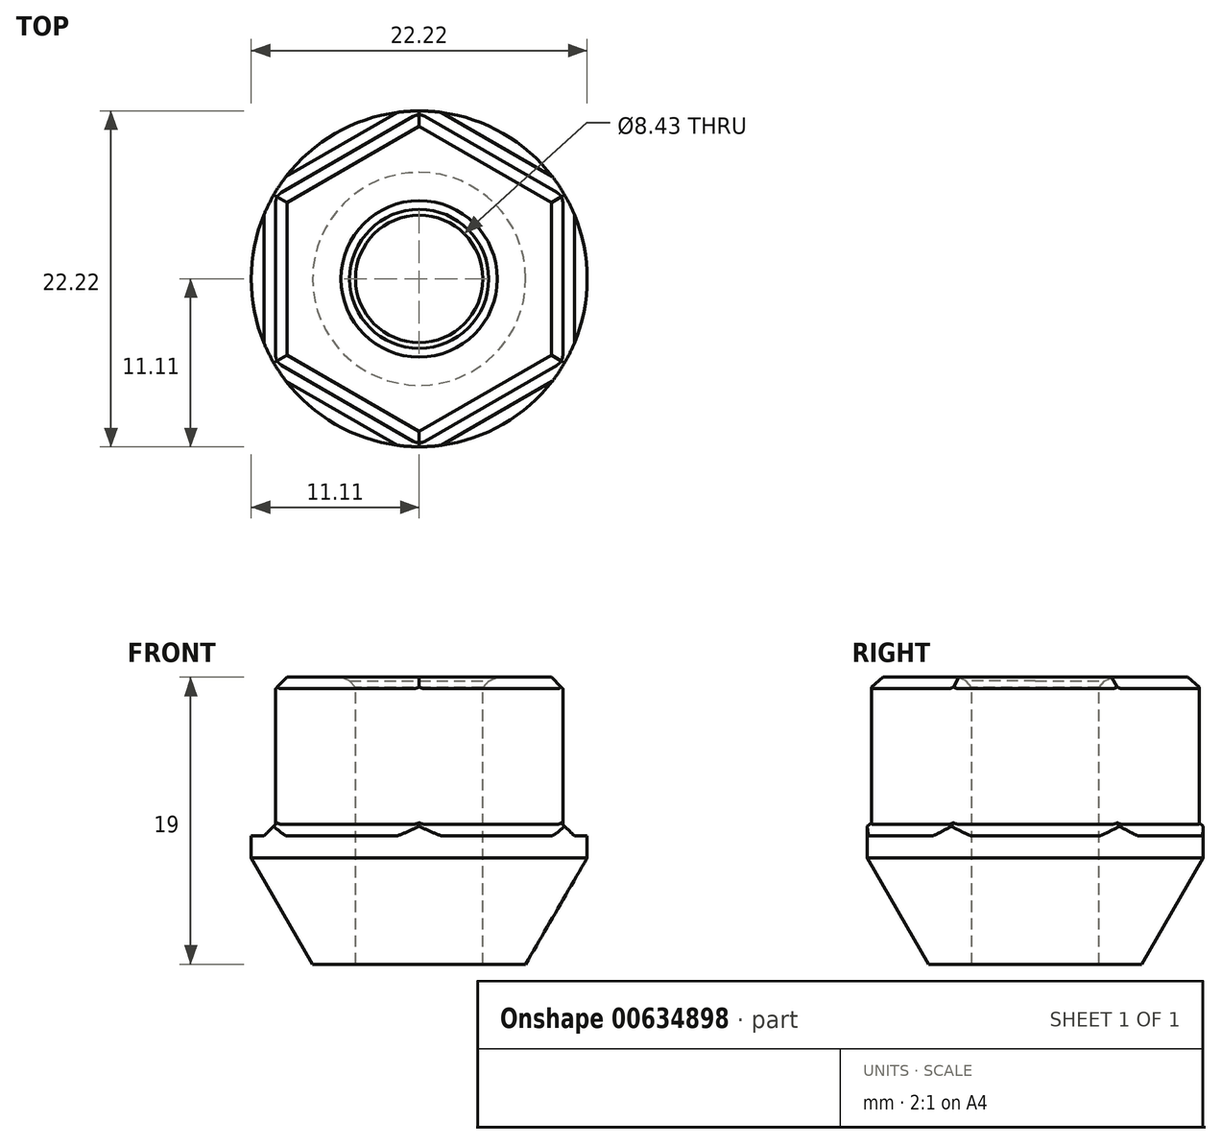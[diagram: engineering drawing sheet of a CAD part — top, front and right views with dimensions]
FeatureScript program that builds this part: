
annotation { "Feature Type Name" : "Feature", "Feature Type Description" : "" }
export const myFeature = defineFeature(function(context is Context, id is Id, definition is map)
    precondition{}
    {
        {
            var Q0;
            Q0=qCreatedBy(makeId("Top.planeOp"),FACE);
            var sketch = newSketch(context, id + "F0", { "sketchPlane" : qUnion([Q0])});
            skCircle(sketch, "E0.cCircle", {"center": v(0, 0) * mm, "radius": 9.5 * mm, "construction": true});
            skLineSegment(sketch, "E0.0", {"start": v(9.5, 5.48) * mm, "end": v(9.5, -5.48) * mm});
            skLineSegment(sketch, "E0.1", {"start": v(9.5, -5.48) * mm, "end": v(0, -10.97) * mm});
            skLineSegment(sketch, "E0.2", {"start": v(0, -10.97) * mm, "end": v(-9.5, -5.48) * mm});
            skLineSegment(sketch, "E0.3", {"start": v(-9.5, -5.48) * mm, "end": v(-9.5, 5.48) * mm});
            skLineSegment(sketch, "E0.4", {"start": v(-9.5, 5.48) * mm, "end": v(0, 10.97) * mm});
            skLineSegment(sketch, "E0.5", {"start": v(0, 10.97) * mm, "end": v(9.5, 5.48) * mm});
            skPoint(sketch, "E0.0.midPoint", {"position": v(9.5, 0) * mm});
            skSolve(sketch);
        }
        {
            var Q0;
            Q0 = qSketchRegion(id + "F0", true);
            extrude(context, id + "F1", {"entities" : qUnion([Q0]), "oppositeDirection" : true, "depth" : 19 * mm, "offsetDistance" : 25.4 * mm});
        }
        {
            var Q0;
            Q0=sQuery(id+"F0.wireOp",VERTEX,"E0.cCircle.center");
            var Q1;
            Q1=makeQuery(id+"F1.opExtrude","SWEPT_BODY",BODY,{"disambiguationData":[OSD([sQuery(id+"F0.wireOp",EDGE,"E0.0"),sQuery(id+"F0.wireOp",EDGE,"E0.1"),sQuery(id+"F0.wireOp",EDGE,"E0.2"),sQuery(id+"F0.wireOp",EDGE,"E0.3"),sQuery(id+"F0.wireOp",EDGE,"E0.4"),sQuery(id+"F0.wireOp",EDGE,"E0.5")])]});
            hole(context, id + "F2", {"style" : HoleStyle.C_SINK, "endStyle" : HoleEndStyle.THROUGH, "holeDiameter" : 8.43 * mm, "cSinkDiameter" : 9.65 * mm, "cSinkAngle" : 82 * degree, "majorDiameter" : 9.52 * mm, "isTappedThrough" : true, "tappedDepth" : 3.56 * mm, "tapClearance" : 3, "startFromSketch" : true, "locations" : qUnion([Q0]), "scope" : qUnion([Q1])});
        }
        {
            var Q0;
            Q0=makeQuery(id+"F1.opExtrude","CAP_FACE",FACE,{"disambiguationData":[OSD([sQuery(id+"F0.wireOp",EDGE,"E0.0"),sQuery(id+"F0.wireOp",EDGE,"E0.1"),sQuery(id+"F0.wireOp",EDGE,"E0.2"),sQuery(id+"F0.wireOp",EDGE,"E0.3"),sQuery(id+"F0.wireOp",EDGE,"E0.4"),sQuery(id+"F0.wireOp",EDGE,"E0.5")])],"isStart":false});
            var sketch = newSketch(context, id + "F3", { "sketchPlane" : qUnion([Q0])});
            skCircle(sketch, "E1", {"center": v(0, 0) * mm, "radius": 11.11 * mm});
            skCircle(sketch, "E2.0", {"center": v(0, 0) * mm, "radius": 4.22 * mm});
            skSolve(sketch);
        }
        {
            var Q0;
            Q0 = qSketchRegion(id + "F3", true);
            extrude(context, id + "F4", {"entities" : qUnion([Q0]), "operationType" : NewBodyOperationType.ADD, "oppositeDirection" : true, "depth" : 8.5 * mm, "offsetDistance" : 25.4 * mm});
        }
        {
            var Q0;
            Q0=makeQuery(id+"F4.opExtrude","CAP_EDGE",EDGE,{"disambiguationData":[OSD([sQuery(id+"F3.wireOp",EDGE,"E1")])],"isStart":true});
            chamfer(context, id + "F5", {"entities" : qUnion([Q0]), "chamferType" : ChamferType.OFFSET_ANGLE, "width" : 4.06 * mm, "oppositeDirection" : false, "angle" : 60 * degree, "tangentPropagation" : true});
        }
        {
            var Q0;
            Q0=makeQuery(id+"F1.opExtrude","CAP_FACE",FACE,{"disambiguationData":[OSD([sQuery(id+"F0.wireOp",EDGE,"E0.0"),sQuery(id+"F0.wireOp",EDGE,"E0.1"),sQuery(id+"F0.wireOp",EDGE,"E0.2"),sQuery(id+"F0.wireOp",EDGE,"E0.3"),sQuery(id+"F0.wireOp",EDGE,"E0.4"),sQuery(id+"F0.wireOp",EDGE,"E0.5")])],"isStart":true});
            chamfer(context, id + "F6", {"entities" : qUnion([Q0]), "width" : 0.76 * mm, "tangentPropagation" : true});
        }
        {
            var Q0;
            Q0=makeQuery(id+"F4.boolean.opBoolean","INTERSECT",EDGE,{"derivedFrom":[makeQuery(id+"F1.opExtrude","SWEPT_FACE",FACE,{"disambiguationData":[OSD([sQuery(id+"F0.wireOp",EDGE,"E0.2")])]}),makeQuery(id+"F4.opExtrude","CAP_FACE",FACE,{"disambiguationData":[OSD([sQuery(id+"F3.wireOp",EDGE,"E1"),sQuery(id+"F3.wireOp",EDGE,"E2.0")])],"isStart":false})]});
            var Q1;
            Q1=makeQuery(id+"F4.boolean.opBoolean","INTERSECT",EDGE,{"derivedFrom":[makeQuery(id+"F1.opExtrude","SWEPT_FACE",FACE,{"disambiguationData":[OSD([sQuery(id+"F0.wireOp",EDGE,"E0.1")])]}),makeQuery(id+"F4.opExtrude","CAP_FACE",FACE,{"disambiguationData":[OSD([sQuery(id+"F3.wireOp",EDGE,"E1"),sQuery(id+"F3.wireOp",EDGE,"E2.0")])],"isStart":false})]});
            var Q2;
            Q2=makeQuery(id+"F4.boolean.opBoolean","INTERSECT",EDGE,{"derivedFrom":[makeQuery(id+"F1.opExtrude","SWEPT_FACE",FACE,{"disambiguationData":[OSD([sQuery(id+"F0.wireOp",EDGE,"E0.0")])]}),makeQuery(id+"F4.opExtrude","CAP_FACE",FACE,{"disambiguationData":[OSD([sQuery(id+"F3.wireOp",EDGE,"E1"),sQuery(id+"F3.wireOp",EDGE,"E2.0")])],"isStart":false})]});
            var Q3;
            Q3=makeQuery(id+"F4.boolean.opBoolean","INTERSECT",EDGE,{"derivedFrom":[makeQuery(id+"F1.opExtrude","SWEPT_FACE",FACE,{"disambiguationData":[OSD([sQuery(id+"F0.wireOp",EDGE,"E0.5")])]}),makeQuery(id+"F4.opExtrude","CAP_FACE",FACE,{"disambiguationData":[OSD([sQuery(id+"F3.wireOp",EDGE,"E1"),sQuery(id+"F3.wireOp",EDGE,"E2.0")])],"isStart":false})]});
            var Q4;
            Q4=makeQuery(id+"F4.boolean.opBoolean","INTERSECT",EDGE,{"derivedFrom":[makeQuery(id+"F1.opExtrude","SWEPT_FACE",FACE,{"disambiguationData":[OSD([sQuery(id+"F0.wireOp",EDGE,"E0.4")])]}),makeQuery(id+"F4.opExtrude","CAP_FACE",FACE,{"disambiguationData":[OSD([sQuery(id+"F3.wireOp",EDGE,"E1"),sQuery(id+"F3.wireOp",EDGE,"E2.0")])],"isStart":false})]});
            var Q5;
            Q5=makeQuery(id+"F4.boolean.opBoolean","INTERSECT",EDGE,{"derivedFrom":[makeQuery(id+"F1.opExtrude","SWEPT_FACE",FACE,{"disambiguationData":[OSD([sQuery(id+"F0.wireOp",EDGE,"E0.3")])]}),makeQuery(id+"F4.opExtrude","CAP_FACE",FACE,{"disambiguationData":[OSD([sQuery(id+"F3.wireOp",EDGE,"E1"),sQuery(id+"F3.wireOp",EDGE,"E2.0")])],"isStart":false})]});
            chamfer(context, id + "F7", {"entities" : qUnion([Q0, Q1, Q2, Q3, Q4, Q5]), "width" : 0.76 * mm, "tangentPropagation" : true});
        }
        {
            var Q0;
            Q0=makeQuery(id+"F1.opExtrude","SWEPT_EDGE",EDGE,{"disambiguationData":[OSD([sQuery(id+"F0.wireOp",EDGE,"E0.0"),sQuery(id+"F0.wireOp",EDGE,"E0.1")])]});
            var Q1;
            Q1=makeQuery(id+"F1.opExtrude","SWEPT_EDGE",EDGE,{"disambiguationData":[OSD([sQuery(id+"F0.wireOp",EDGE,"E0.1"),sQuery(id+"F0.wireOp",EDGE,"E0.2")])]});
            var Q2;
            Q2=makeQuery(id+"F1.opExtrude","SWEPT_EDGE",EDGE,{"disambiguationData":[OSD([sQuery(id+"F0.wireOp",EDGE,"E0.2"),sQuery(id+"F0.wireOp",EDGE,"E0.3")])]});
            var Q3;
            Q3=makeQuery(id+"F1.opExtrude","SWEPT_EDGE",EDGE,{"disambiguationData":[OSD([sQuery(id+"F0.wireOp",EDGE,"E0.3"),sQuery(id+"F0.wireOp",EDGE,"E0.4")])]});
            var Q4;
            Q4=makeQuery(id+"F1.opExtrude","SWEPT_EDGE",EDGE,{"disambiguationData":[OSD([sQuery(id+"F0.wireOp",EDGE,"E0.4"),sQuery(id+"F0.wireOp",EDGE,"E0.5")])]});
            var Q5;
            Q5=makeQuery(id+"F1.opExtrude","SWEPT_EDGE",EDGE,{"disambiguationData":[OSD([sQuery(id+"F0.wireOp",EDGE,"E0.0"),sQuery(id+"F0.wireOp",EDGE,"E0.5")])]});
            fillet(context, id + "F8", {"entities" : qUnion([Q0, Q1, Q2, Q3, Q4, Q5]), "radius" : 0.76 * mm, "tangentPropagation" : true, "allowEdgeOverflow" : false});
        }
    });
